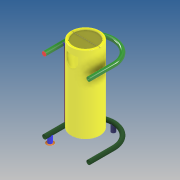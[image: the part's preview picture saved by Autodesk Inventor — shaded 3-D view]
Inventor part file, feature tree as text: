
AUTODESK INVENTOR PART (.ipt)
format: ipt  version: 2021.1 (Build 251245000, 245)  size: 867,328 bytes
history: native  units: mm
features: other x14, sketch x13, extrude x11, fillet x6, hole x6, plane x6, pattern_circular x5, shell x2, revolve x1, sweep x1, pattern_linear x1, chamfer x1
ambient origin geometry x8: Origin, YZ Plane, XZ Plane, XY Plane, X Axis, Y Axis, Z Axis, Center Point
bodies: Body1 (feature_tree), Body2 (feature_tree), Body3 (feature_tree), Body4 (feature_tree), Body5 (feature_tree), Body6 (feature_tree), Body7 (feature_tree), Body8 (feature_tree), Body9 (feature_tree), Body10 (feature_tree), Body11 (feature_tree)
feature tree (67):
  other  "Bin"
  revolve  "Revolution1"  [1 undecoded]
  fillet  "Fillet1"  Radius=25.0mm
  shell  "Shell1"  Thickness=300.0mm
  hole  "Holes Sketch"  [1 undecoded]
  hole  "Hole1"  [1 undecoded]
  pattern_circular  "Circular Pattern1"  Count=3  [1 undecoded]
  hole  "Hole2"  [1 undecoded]
  pattern_circular  "Circular Pattern2"  Count=3  [1 undecoded]
  hole  "Hole3"  [1 undecoded]
  pattern_circular  "Circular Pattern3"  Count=40 Angle=360.0deg
  hole  "Hole4"  [1 undecoded]
  pattern_circular  "Circular Pattern4"  Count=20 Angle=360.0deg
  hole  "Hole5"  [1 undecoded]
  pattern_circular  "Circular Pattern5"  Count=15  [1 undecoded]
  sketch  "Sketch3"  dims[d4=90.0deg d5=5.0mm]
  plane  "Work Plane1"
  sweep  "Sweep1"
  shell  "Shell2"  Thickness=42.8mm
  fillet  "Fillet3"  Radius=60.0mm
  pattern_linear  "Rectangular Pattern1"  Spacing1=0.0mm  [1 undecoded]
  plane  "Work Plane2"
  extrude  "Extrusion1"  Depth=1.0mm
  other  "Swivel Sketch"
  plane  "Work Plane3"
  plane  "Work Plane4"
  extrude  "Extrusion3"  Depth=1.0mm
  extrude  "Extrusion2"  Depth=1.0mm
  extrude  "Extrusion4"  Depth=10.0mm TaperAngle=0.0deg
  fillet  "Fillet2"  Radius=4.0mm
  plane  "Work Plane5"
  extrude  "Extrusion5"  Depth=1.0mm
  fillet  "Fillet4"  Radius=3.0mm
  extrude  "Extrusion6"  Depth=10.0mm TaperAngle=0.0deg
  fillet  "Fillet5"  Radius=4.0mm
  fillet  "Fillet6"  Radius=34.0mm
  extrude  "Extrusion7"  Depth=1.0mm
  extrude  "Extrusion8"  Depth=10.0mm TaperAngle=0.0deg
  other  "Leg Sketch"
  plane  "Work Plane6"
  sketch  "Sketch15"  dims[d52=5.0mm]
  extrude  "Extrusion9"  Depth=1.0mm
  extrude  "Extrusion10"  Depth=1.0mm TaperAngle=0.0deg
  extrude  "Extrusion11"  Depth=1.0mm
  chamfer  "Chamfer1"  Distance=1.0mm
  sketch  "Sketch1"  dims[d0=800.0mm d1=15.0mm d2=25.0mm d3=300.0mm]
  sketch  "Sketch4"  dims[d6=3.0mm d7=8.0mm d8=30.0mm]
  other  "Upper Frame"
  other  "Pattern of Upper Frame:1"
  other  "Duplicate Frame (Lower)"
  sketch  "Sketch5"  dims[d9=30.0mm d10=30.0mm d11=30.0mm]
  other  "Vertical Frame"
  sketch  "Sketch7"  dims[d12=5.0mm d13=6.0mm d14=4.0mm d15=2.0mm d16=90.0deg d17=8.0mm d18=20.594885mm d19=500.0mm d20=360.0deg]
  other  "Swivel Cup"
  sketch  "Sketch8"  dims[d22=5.0mm]
  other  "Swivel"
  sketch  "Sketch9"  dims[d23=6.0mm d24=4.0mm d25=2.0mm d26=90.0deg d27=8.0mm d28=20.594885mm d29=400.0mm d30=360.0deg]
  other  "Tube Cap"
  sketch  "Sketch10"  dims[d32=5.0mm]
  other  "Bin Lid"
  sketch  "Sketch11"  dims[d33=6.0mm d34=4.0mm d35=2.0mm d36=90.0deg d37=8.0mm d38=20.594885mm d39=300.0mm d40=360.0deg]
  sketch  "Sketch12"  dims[d42=5.0mm]
  sketch  "Sketch13"  dims[d43=6.0mm d44=4.0mm d45=2.0mm d46=90.0deg d47=8.0mm d48=20.594885mm d49=200.0mm d50=360.0deg]
  other  "Front Leg"
  other  "Back Leg"
  sketch  "Sketch16"  dims[d53=6.0mm d54=4.0mm d55=2.0mm d56=90.0deg d57=8.0mm d58=20.594885mm d59=100.0mm d60=360.0deg d62=150.0mm d63=460.0mm d64=42.8mm d65=60.0mm d66=0.0mm d67=0.0mm d68=200.0mm d69=3.0mm d70=20.0mm d72=750.0mm d73=10.0mm d74=0.0mm d75=4.0mm d76=35.0mm d78=3.0mm d79=10.0mm d80=0.0mm d81=4.0mm d82=34.0mm d83=3.0mm d84=10.0mm d85=0.0mm d86=20.0mm d87=3.0mm d88=0.0mm d89=1.0mm d90=1.0mm d91=-8.0mm d92=2.0mm d93=3.0mm d94=0.0mm d95=1.0mm d96=6.0mm d97=0.5mm d98=306.0mm d99=0.0mm d100=2.0mm d101=1.0mm d102=0.25mm d103=0.0mm d104=0.0mm d105=65.0mm d106=60.0mm d107=120.0mm d108=0.0mm d109=0.0mm d110=60.0mm d111=60.0mm d112=306.0mm d113=0.0mm d114=306.0mm d115=0.0mm d116=15.0mm d117=3.0mm d118=0.0mm d119=1.0mm d120=2.0mm d121=45.0deg]
  other  "Foot"
note: 11 required parameter values undecoded (feature->parameter linkage not recoverable at this tier; creation-order binding heuristic only, values carry confidence <= 0.55)